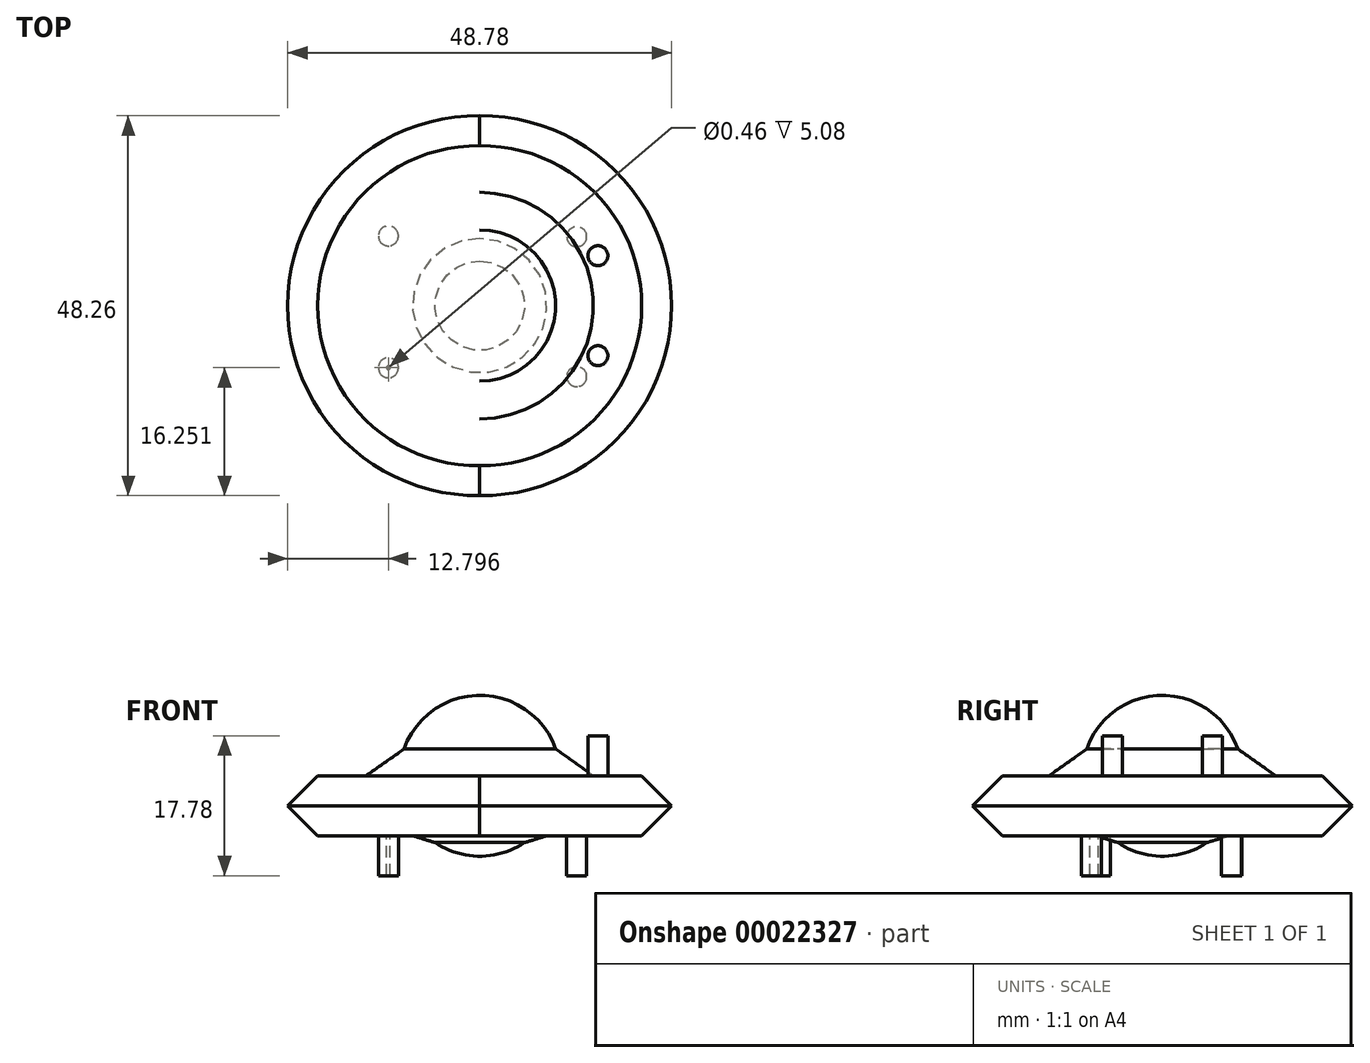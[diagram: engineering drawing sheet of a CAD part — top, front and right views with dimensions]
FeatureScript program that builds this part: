
annotation { "Feature Type Name" : "Feature", "Feature Type Description" : "" }
export const myFeature = defineFeature(function(context is Context, id is Id, definition is map)
    precondition{}
    {
        {
            var Q0;
            Q0=qCreatedBy(makeId("Top.planeOp"),FACE);
            var sketch = newSketch(context, id + "F0", { "sketchPlane" : qUnion([Q0])});
            skLineSegment(sketch, "E0", {"start": v(0, 25.55) * mm, "end": v(0, -25.25) * mm});
            skArc(sketch, "E1", {"start": v(0, 25.55) * mm, "mid": v(-25.66, 0.15) * mm, "end": v(0, -25.25) * mm});
            skArc(sketch, "E2.MirrorCS", {"start": v(0, 25.55) * mm, "mid": v(25.66, 0.15) * mm, "end": v(0, -25.25) * mm});
            skSolve(sketch);
        }
        {
            var Q0;
            Q0=makeQuery(id+"F0.imprint","IMPRINT",FACE,{"disambiguationData":[TD([[makeQuery(id+"F0.imprint","IMPRINT",EDGE,{"derivedFrom":sQuery(id+"F0.wireOp",EDGE,"E0")}),1.0]])]});
            var Q1;
            Q1=makeQuery(id+"F0.imprint","IMPRINT",FACE,{"disambiguationData":[TD([[makeQuery(id+"F0.imprint","IMPRINT",EDGE,{"derivedFrom":sQuery(id+"F0.wireOp",EDGE,"E0")}),-1.0]])]});
            extrude(context, id + "F1", {"entities" : qUnion([Q0, Q1]), "depth" : 5.08 * mm});
        }
        {
            var Q0;
            Q0=makeQuery(id+"F1.opExtrude","CAP_FACE",FACE,{"disambiguationData":[OSD([sQuery(id+"F0.wireOp",EDGE,"E1"),sQuery(id+"F0.wireOp",EDGE,"E2.MirrorCS")])],"isStart":false});
            extrude(context, id + "F2", {"entities" : qUnion([Q0]), "operationType" : NewBodyOperationType.ADD, "depth" : 2.54 * mm});
        }
        {
            var Q0;
            Q0=makeQuery(id+"F2.opExtrude","CAP_FACE",FACE,{"disambiguationData":[OSD([sQuery(id+"F0.wireOp",EDGE,"E1"),sQuery(id+"F0.wireOp",EDGE,"E2.MirrorCS")])],"isStart":false});
            var sketch = newSketch(context, id + "F3", { "sketchPlane" : qUnion([Q0])});
            skLineSegment(sketch, "E3", {"start": v(0.01, -20.17) * mm, "end": v(0.01, 20.47) * mm});
            skArc(sketch, "E4", {"start": v(0.01, 10.33) * mm, "mid": v(-10.2, 0.17) * mm, "end": v(0.01, -9.99) * mm});
            skSolve(sketch);
        }
        {
            var Q0;
            {var subQ0=sQuery(id+"F3.wireOp",EDGE,"E4");Q0=makeQuery(id+"F3.imprint","IMPRINT",FACE,{"disambiguationData":[TD([[makeQuery(id+"F3.imprint","IMPRINT",EDGE,{"derivedFrom":subQ0}),1.0]])]});}
            var Q1;
            Q1=sQuery(id+"F3.wireOp",EDGE,"E3");
            revolve(context, id + "F4", {"operationType" : NewBodyOperationType.ADD, "entities" : qUnion([Q0]), "axis" : qUnion([Q1]), "revolveType" : RevolveType.FULL});
        }
        {
            var Q0;
            Q0=makeQuery(id+"F2.opExtrude","CAP_FACE",FACE,{"disambiguationData":[OSD([sQuery(id+"F0.wireOp",EDGE,"E1"),sQuery(id+"F0.wireOp",EDGE,"E2.MirrorCS")])],"isStart":false});
            chamfer(context, id + "F5", {"entities" : qUnion([Q0]), "width" : 5.08 * mm, "tangentPropagation" : true});
        }
        {
            var Q0;
            Q0=makeQuery(id+"F1.opExtrude","CAP_FACE",FACE,{"disambiguationData":[OSD([sQuery(id+"F0.wireOp",EDGE,"E1"),sQuery(id+"F0.wireOp",EDGE,"E2.MirrorCS")])],"isStart":true});
            chamfer(context, id + "F6", {"entities" : qUnion([Q0]), "width" : 5.08 * mm, "tangentPropagation" : true});
        }
        {
            var Q0;
            Q0=makeQuery(id+"F2.opExtrude","CAP_FACE",FACE,{"disambiguationData":[OSD([sQuery(id+"F0.wireOp",EDGE,"E1"),sQuery(id+"F0.wireOp",EDGE,"E2.MirrorCS")])],"isStart":false});
            var sketch = newSketch(context, id + "F7", { "sketchPlane" : qUnion([Q0])});
            skLineSegment(sketch, "E5", {"start": v(-20.58, 0.15) * mm, "end": v(20.58, 0.15) * mm});
            skCircle(sketch, "E6", {"center": v(15.03, -6.2) * mm, "radius": 1.27 * mm});
            skCircle(sketch, "E7", {"center": v(15.03, 6.5) * mm, "radius": 1.27 * mm});
            skSolve(sketch);
        }
        {
            var Q0;
            Q0=makeQuery(id+"F7.imprint","IMPRINT",FACE,{"disambiguationData":[TD([[makeQuery(id+"F7.imprint","IMPRINT",EDGE,{"derivedFrom":sQuery(id+"F7.wireOp",EDGE,"E7")}),1.0]])]});
            var Q1;
            Q1=makeQuery(id+"F7.imprint","IMPRINT",FACE,{"disambiguationData":[TD([[makeQuery(id+"F7.imprint","IMPRINT",EDGE,{"derivedFrom":sQuery(id+"F7.wireOp",EDGE,"E6")}),1.0]])]});
            extrude(context, id + "F8", {"entities" : qUnion([Q0, Q1]), "operationType" : NewBodyOperationType.ADD, "depth" : 5.08 * mm});
        }
        {
            var Q0;
            Q0=makeQuery(id+"F1.opExtrude","CAP_FACE",FACE,{"disambiguationData":[OSD([sQuery(id+"F0.wireOp",EDGE,"E1"),sQuery(id+"F0.wireOp",EDGE,"E2.MirrorCS")])],"isStart":true});
            var sketch = newSketch(context, id + "F9", { "sketchPlane" : qUnion([Q0])});
            skLineSegment(sketch, "E8", {"start": v(-20.58, -0.15) * mm, "end": v(20.58, 0) * mm});
            skCircle(sketch, "E9", {"center": v(-11.6, -9) * mm, "radius": 1.27 * mm});
            skCircle(sketch, "E10", {"center": v(-11.6, 7.73) * mm, "radius": 0.23 * mm});
            skCircle(sketch, "E11", {"center": v(12.33, -8.92) * mm, "radius": 1.27 * mm});
            skCircle(sketch, "E12", {"center": v(12.33, 8.86) * mm, "radius": 1.27 * mm});
            skCircle(sketch, "E13", {"center": v(-11.6, 7.73) * mm, "radius": 1.27 * mm});
            skSolve(sketch);
        }
        {
            var Q0;
            Q0=makeQuery(id+"F9.imprint","IMPRINT",FACE,{"disambiguationData":[TD([[makeQuery(id+"F9.imprint","IMPRINT",EDGE,{"derivedFrom":sQuery(id+"F9.wireOp",EDGE,"E9")}),1.0]])]});
            var Q1;
            Q1=makeQuery(id+"F9.imprint","IMPRINT",FACE,{"disambiguationData":[TD([[makeQuery(id+"F9.imprint","IMPRINT",EDGE,{"derivedFrom":sQuery(id+"F9.wireOp",EDGE,"E11")}),1.0]])]});
            var Q2;
            Q2=makeQuery(id+"F9.imprint","IMPRINT",FACE,{"disambiguationData":[TD([[makeQuery(id+"F9.imprint","IMPRINT",EDGE,{"derivedFrom":sQuery(id+"F9.wireOp",EDGE,"E10")}),-1.0]])]});
            var Q3;
            Q3=makeQuery(id+"F9.imprint","IMPRINT",FACE,{"disambiguationData":[TD([[makeQuery(id+"F9.imprint","IMPRINT",EDGE,{"derivedFrom":sQuery(id+"F9.wireOp",EDGE,"E12")}),1.0]])]});
            extrude(context, id + "F10", {"entities" : qUnion([Q0, Q1, Q2, Q3]), "operationType" : NewBodyOperationType.ADD, "depth" : 5.08 * mm});
        }
    });
